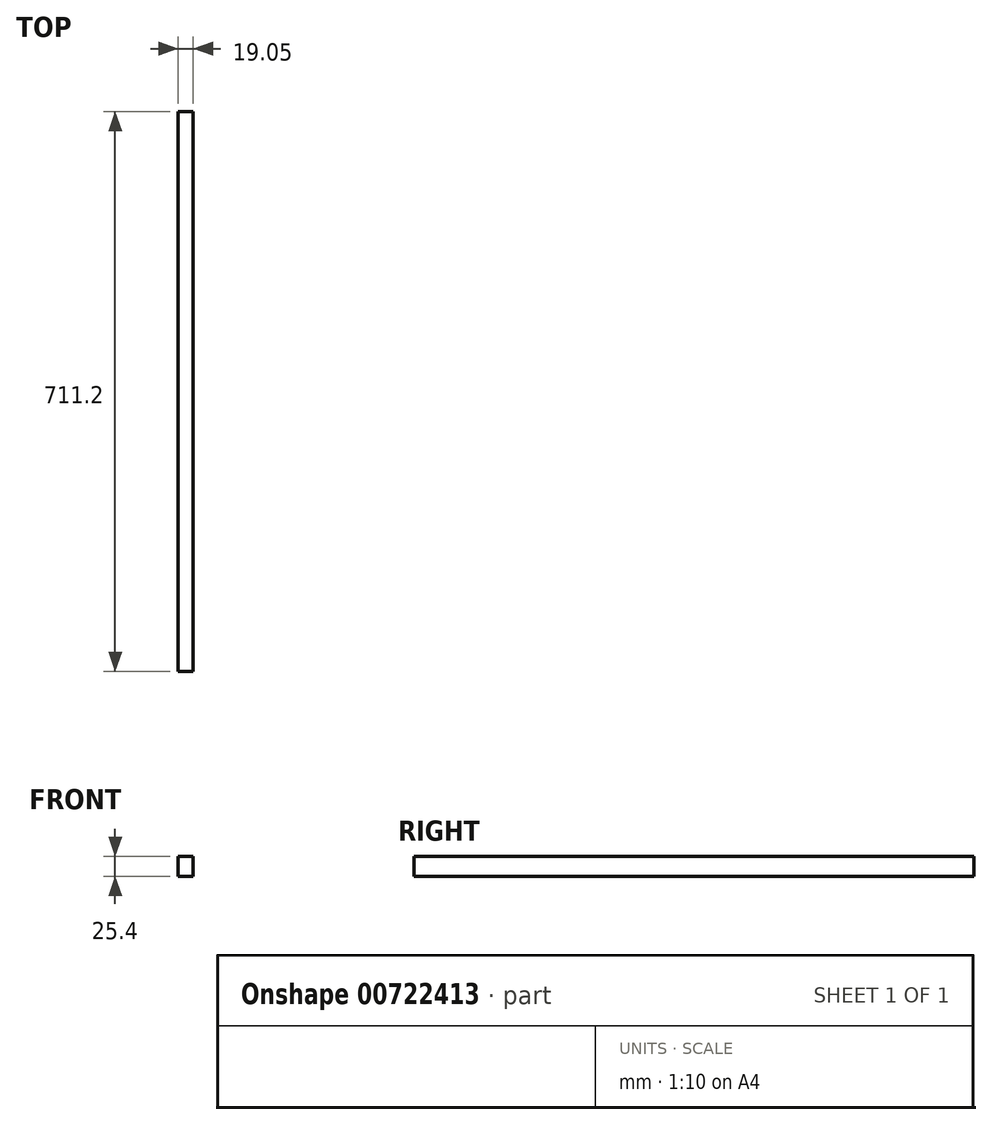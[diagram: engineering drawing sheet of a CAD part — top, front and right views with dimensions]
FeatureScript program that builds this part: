
annotation { "Feature Type Name" : "Feature", "Feature Type Description" : "" }
export const myFeature = defineFeature(function(context is Context, id is Id, definition is map)
    precondition{}
    {
        {
            var Q0;
            Q0=qCreatedBy(makeId("Right.planeOp"),FACE);
            var sketch = newSketch(context, id + "F0", { "sketchPlane" : qUnion([Q0])});
            skLineSegment(sketch, "E0.bottom", {"start": v(355.6, -12.7) * mm, "end": v(-355.6, -12.7) * mm});
            skLineSegment(sketch, "E0.top", {"start": v(355.6, 12.7) * mm, "end": v(-355.6, 12.7) * mm});
            skLineSegment(sketch, "E0.left", {"start": v(355.6, -12.7) * mm, "end": v(355.6, 12.7) * mm});
            skLineSegment(sketch, "E0.right", {"start": v(-355.6, -12.7) * mm, "end": v(-355.6, 12.7) * mm});
            skPoint(sketch, "E0.middle", {"position": v(0, 0) * mm});
            skSolve(sketch);
        }
        {
            var Q0;
            Q0=makeQuery(id+"F0.imprint","IMPRINT",FACE,{"disambiguationData":[TD([[makeQuery(id+"F0.imprint","IMPRINT",EDGE,{"derivedFrom":sQuery(id+"F0.wireOp",EDGE,"E0.bottom")}),-1.0]])]});
            extrude(context, id + "F1", {"entities" : qUnion([Q0]), "depth" : 19.05 * mm, "offsetDistance" : 25.4 * mm});
        }
    });
